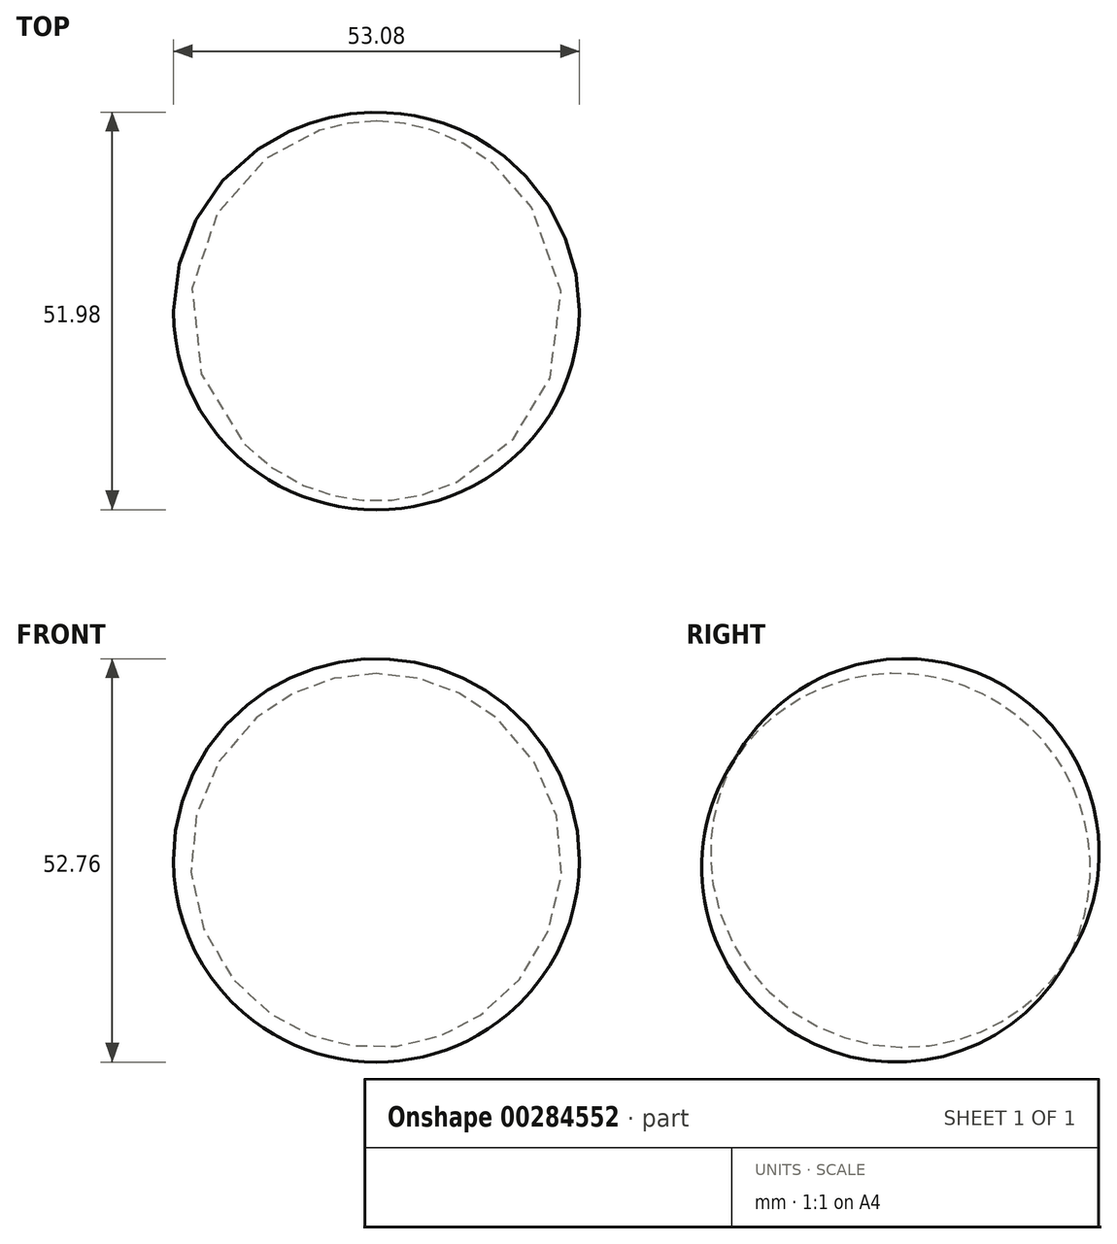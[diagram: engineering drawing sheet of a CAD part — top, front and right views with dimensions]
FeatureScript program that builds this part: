
annotation { "Feature Type Name" : "Feature", "Feature Type Description" : "" }
export const myFeature = defineFeature(function(context is Context, id is Id, definition is map)
    precondition{}
    {
        {
            var Q0;
            Q0=qCreatedBy(makeId("Right.planeOp"),FACE);
            var sketch = newSketch(context, id + "F0", { "sketchPlane" : qUnion([Q0])});
            skArc(sketch, "E0", {"start": v(22.37, -12.06) * mm, "mid": v(13.04, 21.81) * mm, "end": v(-21.21, 14) * mm});
            skLineSegment(sketch, "E1", {"start": v(-21.21, 14) * mm, "end": v(22.37, -12.06) * mm});
            skSolve(sketch);
        }
        {
            var Q0;
            Q0=makeQuery(id+"F0.imprint","IMPRINT",FACE,{"disambiguationData":[TD([[makeQuery(id+"F0.imprint","IMPRINT",EDGE,{"derivedFrom":sQuery(id+"F0.wireOp",EDGE,"E0")}),1.0]])]});
            var Q1;
            Q1=sQuery(id+"F0.wireOp",EDGE,"E1");
            revolve(context, id + "F1", {"entities" : qUnion([Q0]), "axis" : qUnion([Q1]), "revolveType" : RevolveType.FULL});
        }
    });
